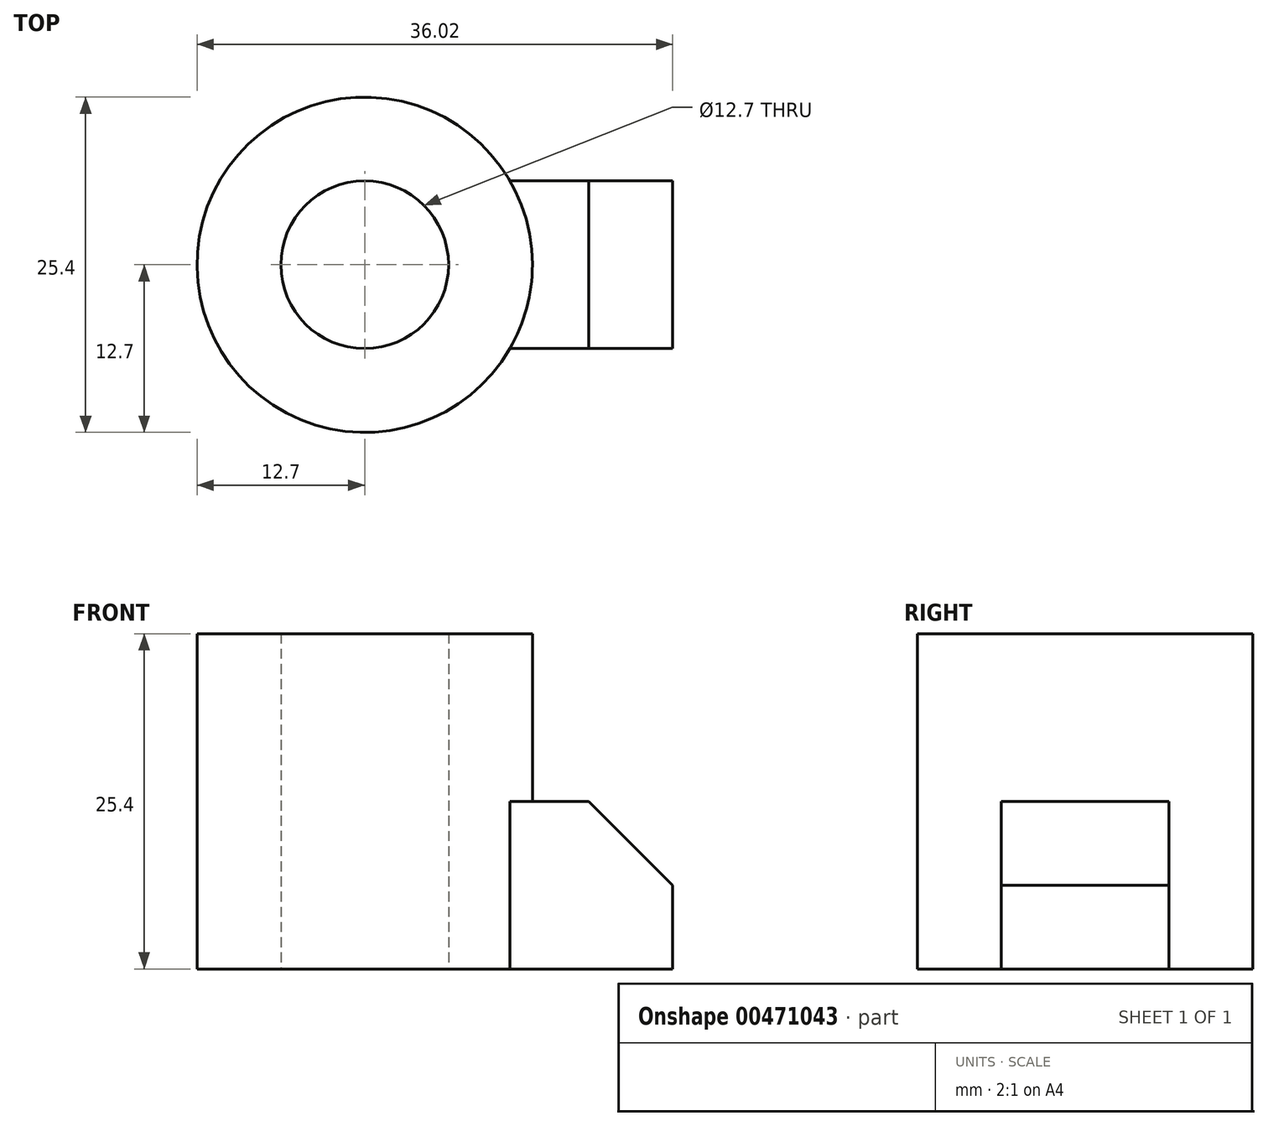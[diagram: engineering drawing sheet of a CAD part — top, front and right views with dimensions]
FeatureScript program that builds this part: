
annotation { "Feature Type Name" : "Feature", "Feature Type Description" : "" }
export const myFeature = defineFeature(function(context is Context, id is Id, definition is map)
    precondition{}
    {
        {
            var Q0;
            Q0=qCreatedBy(makeId("Top.planeOp"),FACE);
            var sketch = newSketch(context, id + "F0", { "sketchPlane" : qUnion([Q0])});
            skCircle(sketch, "E0", {"center": v(0, 0) * mm, "radius": 6.35 * mm});
            skCircle(sketch, "E1.0", {"center": v(0, 0) * mm, "radius": 12.7 * mm});
            skSolve(sketch);
        }
        {
            var Q0;
            Q0 = qSketchRegion(id + "F0", true);
            extrude(context, id + "F1", {"entities" : qUnion([Q0]), "depth" : 25.4 * mm});
        }
        {
            var Q0;
            Q0=qCreatedBy(makeId("Front.planeOp"),FACE);
            var sketch = newSketch(context, id + "F2", { "sketchPlane" : qUnion([Q0])});
            skLineSegment(sketch, "E2.bottom", {"start": v(10.62, 0) * mm, "end": v(23.32, 0) * mm});
            skLineSegment(sketch, "E2.top", {"start": v(10.62, 12.7) * mm, "end": v(23.32, 12.7) * mm});
            skLineSegment(sketch, "E2.left", {"start": v(10.62, 0) * mm, "end": v(10.62, 12.7) * mm});
            skLineSegment(sketch, "E2.right", {"start": v(23.32, 0) * mm, "end": v(23.32, 12.7) * mm});
            skSolve(sketch);
        }
        {
            var Q0;
            Q0 = qSketchRegion(id + "F2", true);
            extrude(context, id + "F3", {"entities" : qUnion([Q0]), "operationType" : NewBodyOperationType.ADD, "endBound" : BoundingType.SYMMETRIC, "depth" : 12.7 * mm});
        }
        {
            var Q0;
            Q0=makeQuery(id+"F3.opExtrude","SWEPT_EDGE",EDGE,{"disambiguationData":[OSD([sQuery(id+"F2.wireOp",EDGE,"E2.top"),sQuery(id+"F2.wireOp",EDGE,"E2.right")])]});
            chamfer(context, id + "F4", {"entities" : qUnion([Q0]), "width" : 6.35 * mm, "tangentPropagation" : true});
        }
    });
